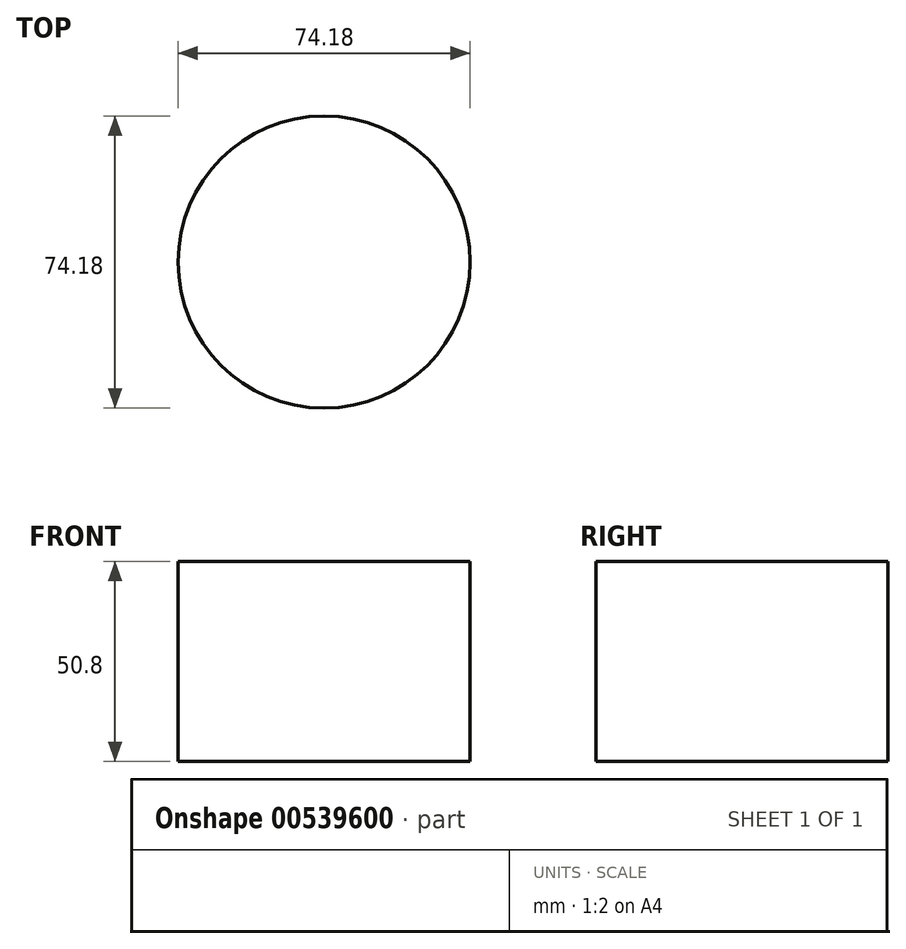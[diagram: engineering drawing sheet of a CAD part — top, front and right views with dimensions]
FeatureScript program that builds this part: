
annotation { "Feature Type Name" : "Feature", "Feature Type Description" : "" }
export const myFeature = defineFeature(function(context is Context, id is Id, definition is map)
    precondition{}
    {
        {
            var Q0;
            Q0=qCreatedBy(makeId("Top.planeOp"),FACE);
            var sketch = newSketch(context, id + "F0", { "sketchPlane" : qUnion([Q0])});
            skCircle(sketch, "E0", {"center": v(0, 0) * mm, "radius": 37.1 * mm});
            skSolve(sketch);
        }
        {
            var Q0;
            Q0=makeQuery(id+"F0.imprint","IMPRINT",FACE,{"disambiguationData":[TD([[makeQuery(id+"F0.imprint","IMPRINT",EDGE,{"derivedFrom":sQuery(id+"F0.wireOp",EDGE,"E0")}),1.0]])]});
            extrude(context, id + "F1", {"entities" : qUnion([Q0]), "depth" : 50.8 * mm, "offsetDistance" : 25.4 * mm});
        }
    });
